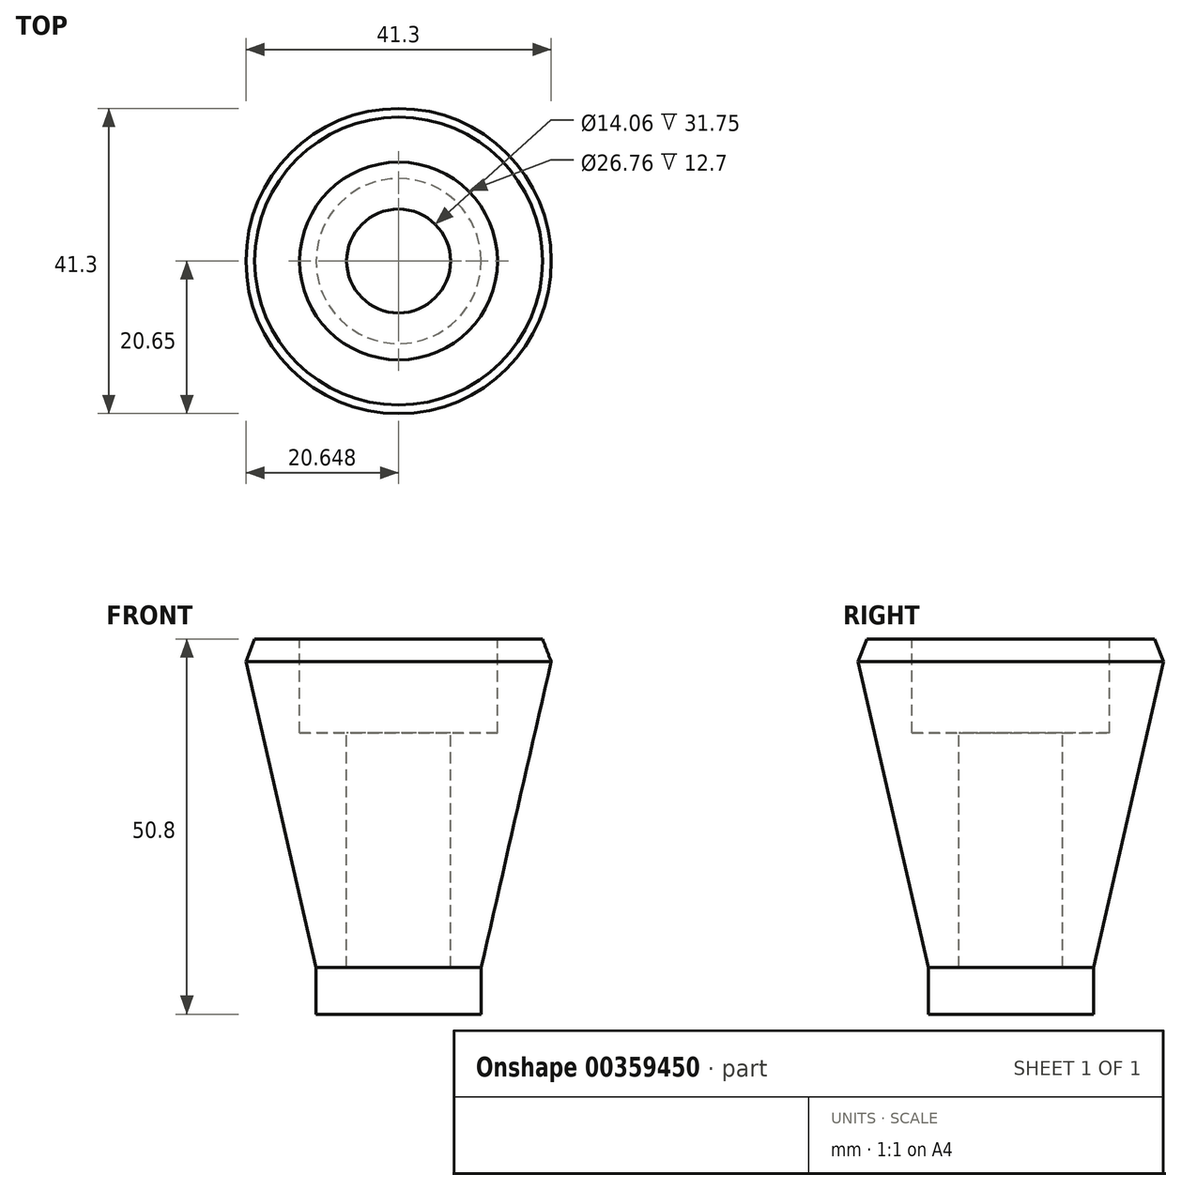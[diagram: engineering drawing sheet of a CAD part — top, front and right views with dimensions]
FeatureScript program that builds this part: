
annotation { "Feature Type Name" : "Feature", "Feature Type Description" : "" }
export const myFeature = defineFeature(function(context is Context, id is Id, definition is map)
    precondition{}
    {
        {
            var Q0;
            Q0=qCreatedBy(makeId("Front.planeOp"),FACE);
            var sketch = newSketch(context, id + "F0", { "sketchPlane" : qUnion([Q0])});
            skLineSegment(sketch, "E0", {"start": v(-38.2, 13.12) * mm, "end": v(-37.02, 16.2) * mm});
            skLineSegment(sketch, "E1", {"start": v(-37.02, 16.2) * mm, "end": v(-30.92, 16.2) * mm});
            skLineSegment(sketch, "E2", {"start": v(-30.92, 16.2) * mm, "end": v(-30.92, 3.5) * mm});
            skLineSegment(sketch, "E3", {"start": v(-30.92, 3.5) * mm, "end": v(-24.57, 3.5) * mm});
            skLineSegment(sketch, "E4", {"start": v(-24.57, 3.5) * mm, "end": v(-24.57, -28.24) * mm});
            skLineSegment(sketch, "E5", {"start": v(-38.2, 13.12) * mm, "end": v(-28.72, -28.24) * mm});
            skLineSegment(sketch, "E6", {"start": v(-28.72, -28.24) * mm, "end": v(-28.72, -34.6) * mm});
            skLineSegment(sketch, "E7", {"start": v(-28.72, -34.6) * mm, "end": v(-17.54, -34.6) * mm});
            skLineSegment(sketch, "E8", {"start": v(-17.54, 49.74) * mm, "end": v(-17.54, -30.99) * mm, "construction": true});
            skLineSegment(sketch, "E9", {"start": v(-24.57, -28.24) * mm, "end": v(-17.54, -28.24) * mm});
            skLineSegment(sketch, "E10", {"start": v(-17.54, -28.24) * mm, "end": v(-17.54, -34.6) * mm});
            skSolve(sketch);
        }
        {
            var Q0;
            Q0=makeQuery(id+"F0.imprint","IMPRINT",FACE,{"disambiguationData":[TD([[makeQuery(id+"F0.imprint","IMPRINT",EDGE,{"derivedFrom":sQuery(id+"F0.wireOp",EDGE,"E0")}),-1.0]])]});
            var Q1;
            Q1=sQuery(id+"F0.wireOp",EDGE,"E8");
            var Q2;
            Q2=sQuery(id+"F0.wireOp",EDGE,"E1");
            var Q3;
            Q3=sQuery(id+"F0.wireOp",EDGE,"E2");
            var Q4;
            Q4=sQuery(id+"F0.wireOp",EDGE,"E0");
            var Q5;
            Q5=sQuery(id+"F0.wireOp",EDGE,"E5");
            var Q6;
            Q6=sQuery(id+"F0.wireOp",EDGE,"E6");
            var Q7;
            Q7=sQuery(id+"F0.wireOp",EDGE,"E7");
            var Q8;
            Q8=sQuery(id+"F0.wireOp",EDGE,"E4");
            var Q9;
            Q9=sQuery(id+"F0.wireOp",EDGE,"E3");
            var Q10;
            Q10=sQuery(id+"F0.wireOp",EDGE,"E8");
            revolve(context, id + "F1", {"entities" : qUnion([Q0]), "surfaceEntities" : qUnion([Q1, Q2, Q3, Q4, Q5, Q6, Q7, Q8, Q9]), "axis" : qUnion([Q10]), "revolveType" : RevolveType.FULL});
        }
    });
